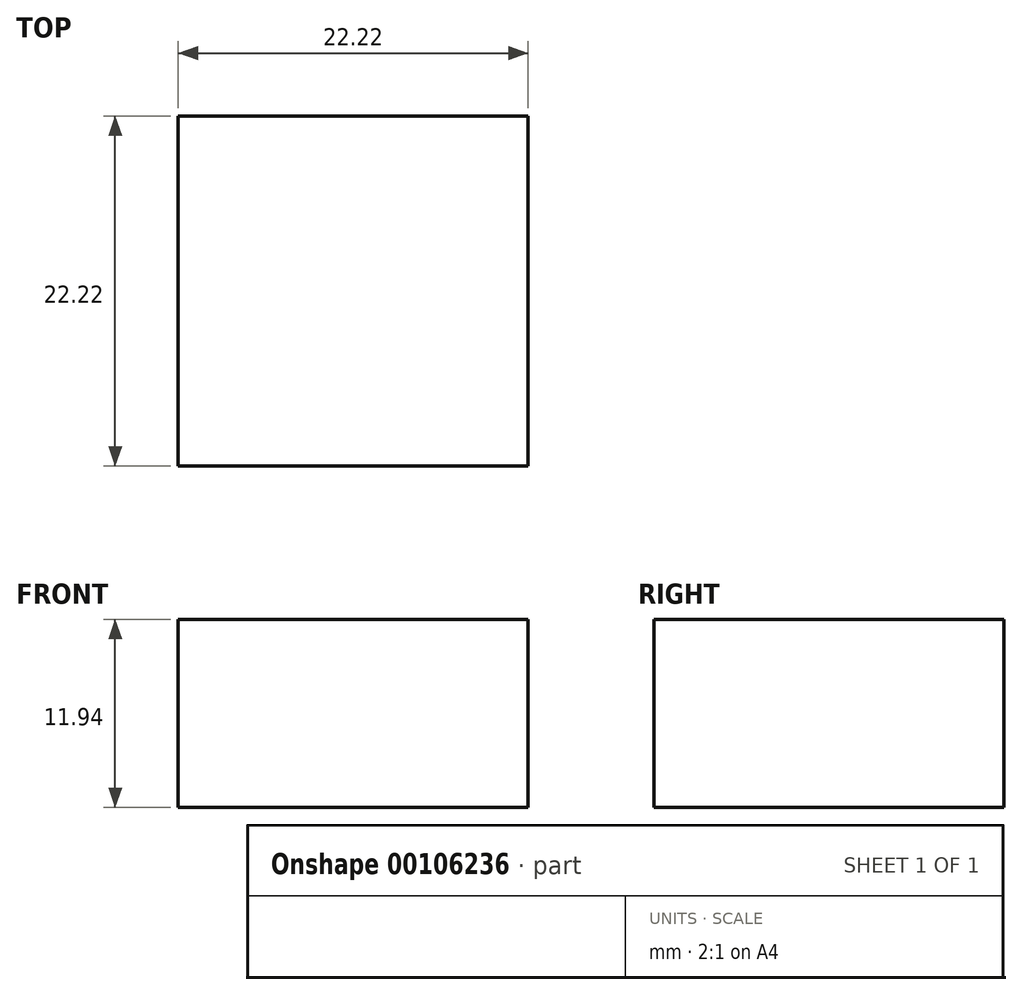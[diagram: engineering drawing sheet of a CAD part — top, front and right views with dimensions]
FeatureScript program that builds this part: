
annotation { "Feature Type Name" : "Feature", "Feature Type Description" : "" }
export const myFeature = defineFeature(function(context is Context, id is Id, definition is map)
    precondition{}
    {
        {
            var Q0;
            Q0=qCreatedBy(makeId("Top.planeOp"),FACE);
            var sketch = newSketch(context, id + "F0", { "sketchPlane" : qUnion([Q0])});
            skLineSegment(sketch, "E0.bottom", {"start": v(-8.33, 18.31) * mm, "end": v(13.9, 18.31) * mm});
            skLineSegment(sketch, "E0.top", {"start": v(-8.33, -3.91) * mm, "end": v(13.9, -3.91) * mm});
            skLineSegment(sketch, "E0.left", {"start": v(-8.33, 18.31) * mm, "end": v(-8.33, -3.91) * mm});
            skLineSegment(sketch, "E0.right", {"start": v(13.9, 18.31) * mm, "end": v(13.9, -3.91) * mm});
            skSolve(sketch);
        }
        {
            var Q0;
            Q0=makeQuery(id+"F0.imprint","IMPRINT",FACE,{"disambiguationData":[TD([[makeQuery(id+"F0.imprint","IMPRINT",EDGE,{"derivedFrom":sQuery(id+"F0.wireOp",EDGE,"E0.bottom")}),-1.0]])]});
            extrude(context, id + "F1", {"entities" : qUnion([Q0]), "depth" : 11.94 * mm});
        }
    });
